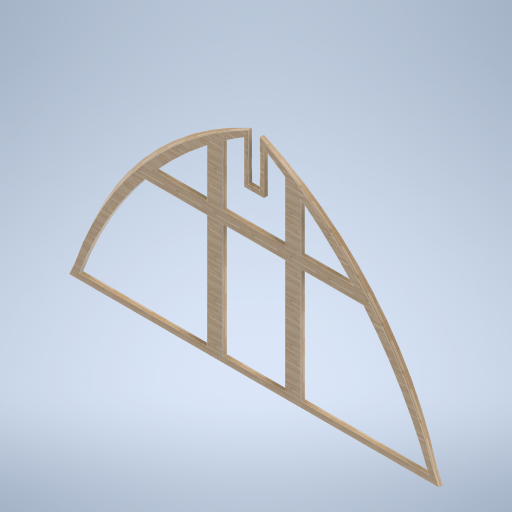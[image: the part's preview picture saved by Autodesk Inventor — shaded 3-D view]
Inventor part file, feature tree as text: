
AUTODESK INVENTOR PART (.ipt)
format: ipt  version: 2024.2 (Build 282272000, 272)  size: 435,712 bytes
history: native  units: mm
features: sketch x4, plane x2, extrude x2, loft x1
ambient origin geometry x8: Origin, YZ Plane, XZ Plane, XY Plane, X Axis, Y Axis, Z Axis, Center Point
bodies: Solid1 (feature_tree)
feature tree (9):
  sketch  "Sketch1"  dims[d2=0.0mm d3=-100.0mm d5=7.0mm]
  plane  "Work Plane2"
  loft  "Loft1"
  extrude  "Extrusion1"  TaperAngle=0.0deg  [1 undecoded]
  extrude  "Extrusion2"  Depth=10000.0mm
  plane  "Work Plane1"
  sketch  "Sketch3"  dims[d6=0.0mm d7=90.0deg d8=0.0mm d9=90.0deg]
  sketch  "Sketch4"  dims[d10=1000.0mm d12=10000.0mm]
  sketch  "Sketch5"  dims[d16=0.0mm d17=0.0mm d20=90.0deg d21=400.0mm d22=90.0deg d23=300.0mm d25=10000.0mm d26=100.0mm d27=0.0mm]
note: 1 required parameter value undecoded (feature->parameter linkage not recoverable at this tier; creation-order binding heuristic only, values carry confidence <= 0.55)
